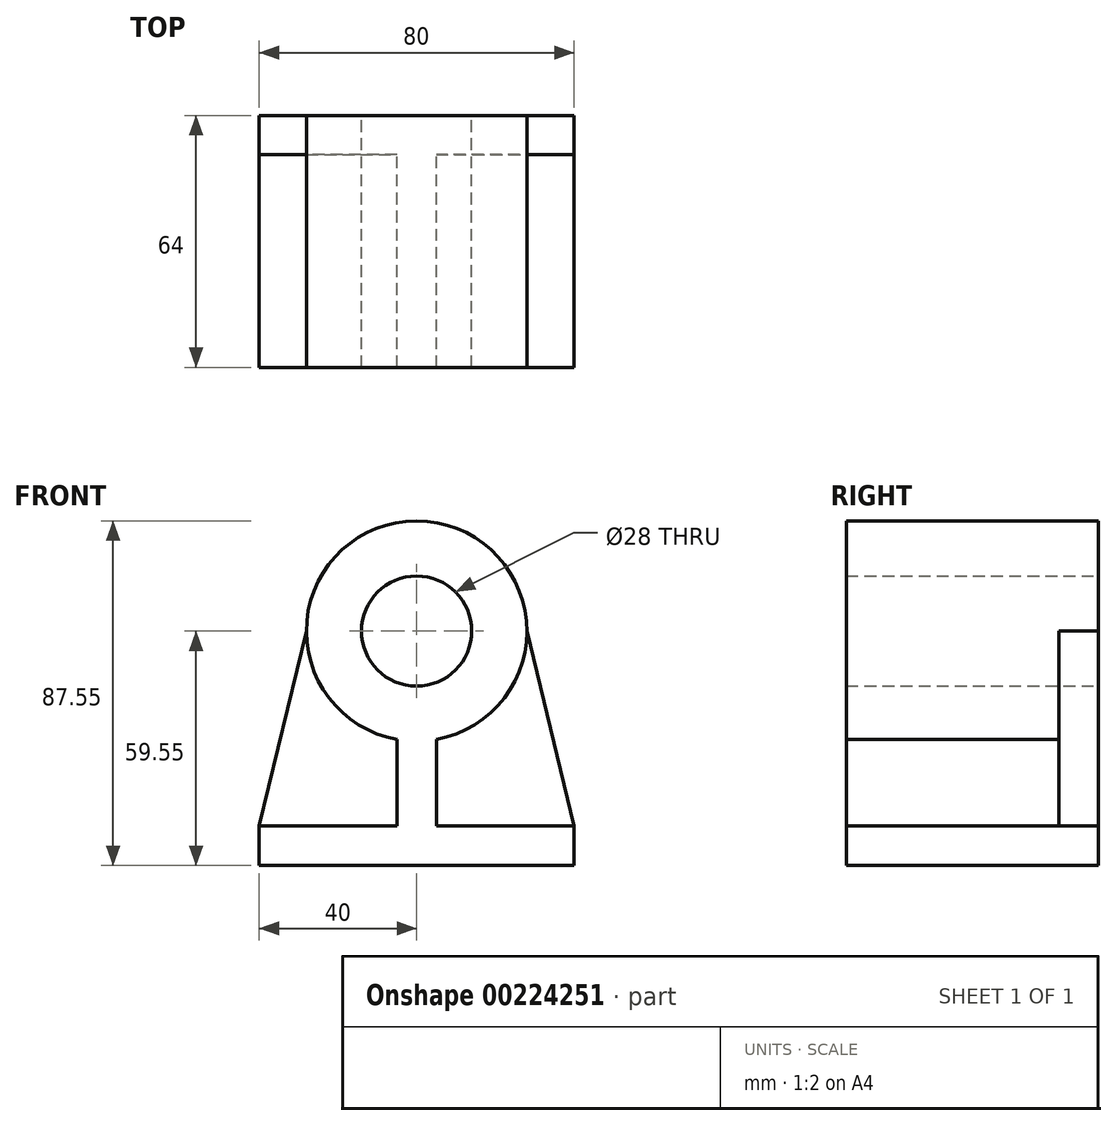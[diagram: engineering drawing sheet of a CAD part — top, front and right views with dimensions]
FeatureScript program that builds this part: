
annotation { "Feature Type Name" : "Feature", "Feature Type Description" : "" }
export const myFeature = defineFeature(function(context is Context, id is Id, definition is map)
    precondition{}
    {
        {
            var Q0;
            Q0=qCreatedBy(makeId("Front.planeOp"),FACE);
            var sketch = newSketch(context, id + "F0", { "sketchPlane" : qUnion([Q0])});
            skLineSegment(sketch, "E0", {"start": v(0, 0) * mm, "end": v(80, 0) * mm});
            skLineSegment(sketch, "E1", {"start": v(80, 0) * mm, "end": v(80, 10) * mm});
            skLineSegment(sketch, "E2", {"start": v(80, 10) * mm, "end": v(45, 10) * mm});
            skLineSegment(sketch, "E3", {"start": v(45, 10) * mm, "end": v(45, 32) * mm});
            skLineSegment(sketch, "E4", {"start": v(35, 32) * mm, "end": v(35, 10) * mm});
            skLineSegment(sketch, "E5", {"start": v(35, 10) * mm, "end": v(0, 10) * mm});
            skLineSegment(sketch, "E6", {"start": v(0, 10) * mm, "end": v(0, 0) * mm});
            skLineSegment(sketch, "E7", {"start": v(40, 82.52) * mm, "end": v(40, -52.82) * mm, "construction": true});
            skArc(sketch, "E8", {"start": v(45, 32) * mm, "mid": v(40, 87.55) * mm, "end": v(35, 32) * mm});
            skCircle(sketch, "E9", {"center": v(40, 59.55) * mm, "radius": 14 * mm});
            skLineSegment(sketch, "E10", {"start": v(-20.93, 59.55) * mm, "end": v(94.82, 59.55) * mm, "construction": true});
            skLineSegment(sketch, "E11", {"start": v(0, 10) * mm, "end": v(12, 59.55) * mm});
            skLineSegment(sketch, "E12", {"start": v(80, 10) * mm, "end": v(68, 59.55) * mm});
            skSolve(sketch);
        }
        {
            var Q0;
            Q0=makeQuery(id+"F0.imprint","IMPRINT",FACE,{"disambiguationData":[TD([[makeQuery(id+"F0.imprint","IMPRINT",EDGE,{"derivedFrom":sQuery(id+"F0.wireOp",EDGE,"E0")}),1.0]])]});
            extrude(context, id + "F1", {"entities" : qUnion([Q0]), "depth" : 64 * mm});
        }
        {
            var Q0;
            {var subQ0=sQuery(id+"F0.wireOp",EDGE,"E4");Q0=makeQuery(id+"F0.imprint","IMPRINT",FACE,{"disambiguationData":[TD([[makeQuery(id+"F0.imprint","IMPRINT",EDGE,{"derivedFrom":subQ0}),-1.0]])]});}
            var Q1;
            Q1=makeQuery(id+"F0.imprint","IMPRINT",FACE,{"disambiguationData":[TD([[makeQuery(id+"F0.imprint","IMPRINT",EDGE,{"derivedFrom":sQuery(id+"F0.wireOp",EDGE,"E2")}),-1.0]])]});
            extrude(context, id + "F2", {"entities" : qUnion([Q0, Q1]), "operationType" : NewBodyOperationType.ADD, "depth" : 10 * mm});
        }
    });
